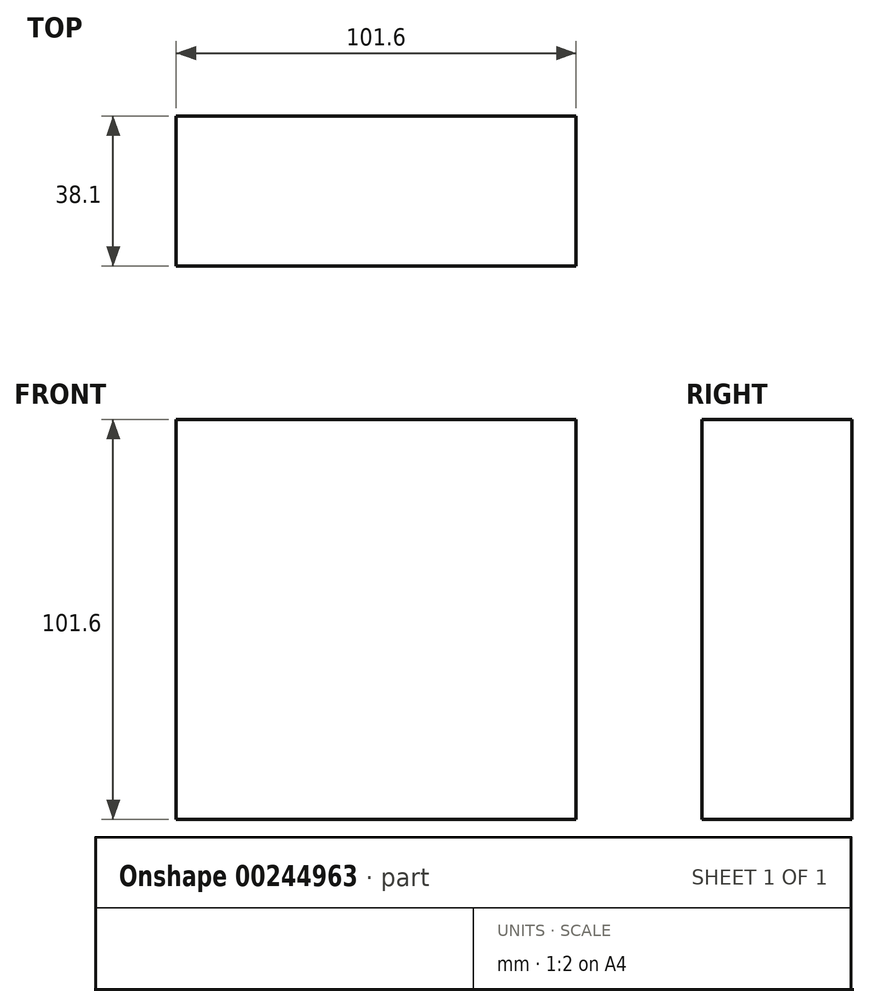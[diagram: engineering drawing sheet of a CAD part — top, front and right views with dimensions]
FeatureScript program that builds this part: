
annotation { "Feature Type Name" : "Feature", "Feature Type Description" : "" }
export const myFeature = defineFeature(function(context is Context, id is Id, definition is map)
    precondition{}
    {
        {
            var Q0;
            Q0=qCreatedBy(makeId("Front.planeOp"),FACE);
            var sketch = newSketch(context, id + "F0", { "sketchPlane" : qUnion([Q0])});
            skLineSegment(sketch, "E0.bottom", {"start": v(-49.53, 56.46) * mm, "end": v(52.07, 56.46) * mm});
            skLineSegment(sketch, "E0.top", {"start": v(-49.53, -45.14) * mm, "end": v(52.07, -45.14) * mm});
            skLineSegment(sketch, "E0.left", {"start": v(-49.53, 56.46) * mm, "end": v(-49.53, -45.14) * mm});
            skLineSegment(sketch, "E0.right", {"start": v(52.07, 56.46) * mm, "end": v(52.07, -45.14) * mm});
            skSolve(sketch);
        }
        {
            var Q0;
            Q0 = qSketchRegion(id + "F0", true);
            extrude(context, id + "F1", {"entities" : qUnion([Q0]), "depth" : 38.1 * mm});
        }
    });
